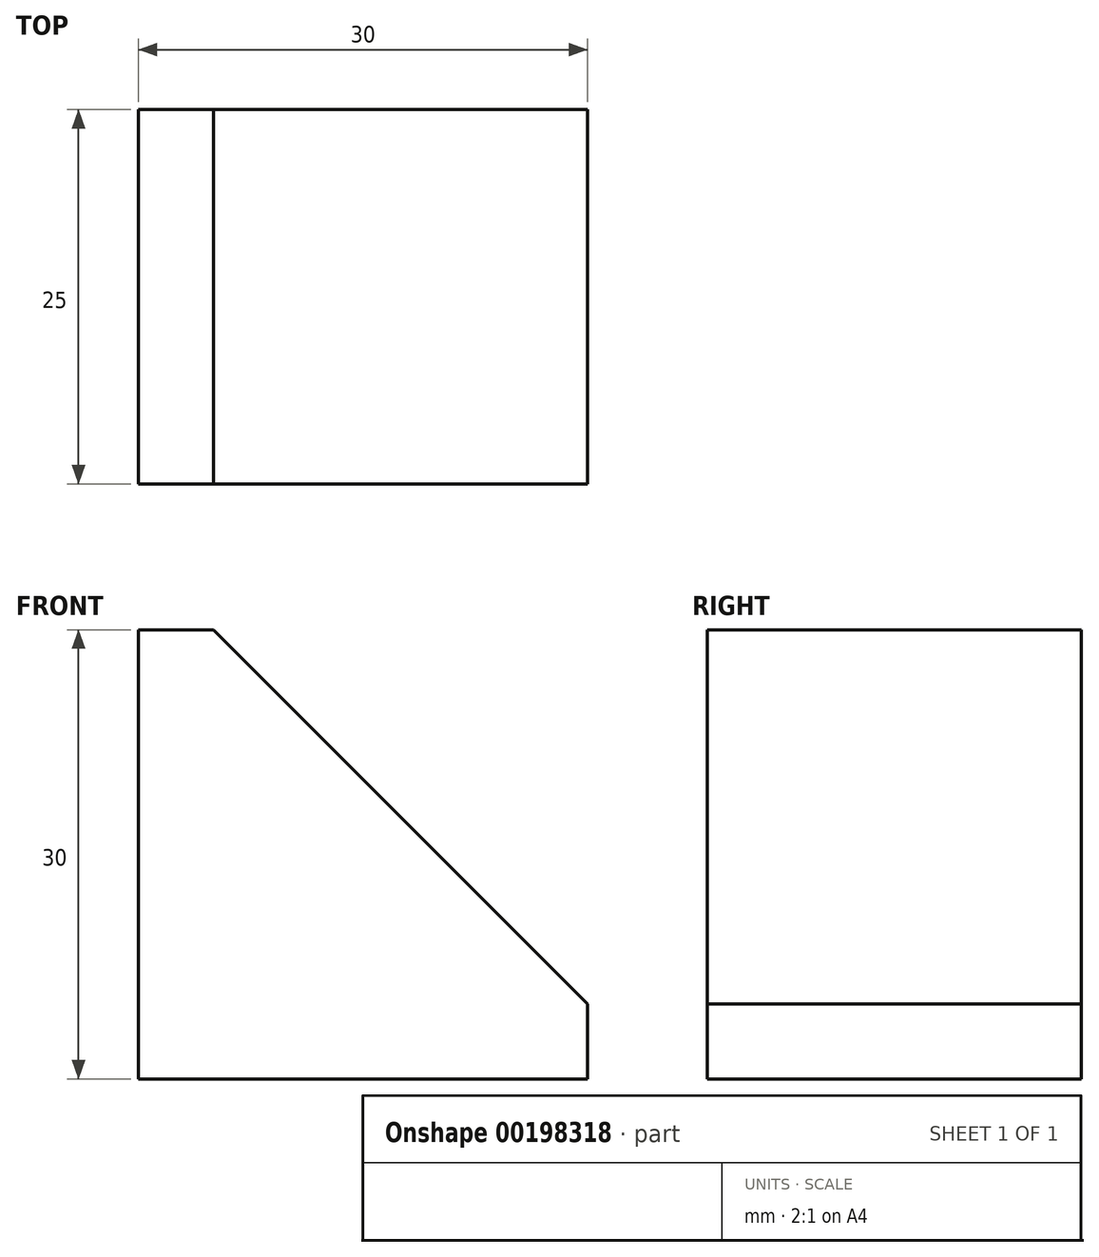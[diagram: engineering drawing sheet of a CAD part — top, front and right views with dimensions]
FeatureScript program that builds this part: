
annotation { "Feature Type Name" : "Feature", "Feature Type Description" : "" }
export const myFeature = defineFeature(function(context is Context, id is Id, definition is map)
    precondition{}
    {
        {
            var Q0;
            Q0=qCreatedBy(makeId("Front.planeOp"),FACE);
            var sketch = newSketch(context, id + "F0", { "sketchPlane" : qUnion([Q0])});
            skLineSegment(sketch, "E0", {"start": v(0, 0) * mm, "end": v(0, 30) * mm});
            skLineSegment(sketch, "E1", {"start": v(0, 30) * mm, "end": v(5, 30) * mm});
            skLineSegment(sketch, "E2", {"start": v(5, 30) * mm, "end": v(30, 5) * mm});
            skLineSegment(sketch, "E3", {"start": v(30, 5) * mm, "end": v(30, 0) * mm});
            skLineSegment(sketch, "E4", {"start": v(30, 0) * mm, "end": v(0, 0) * mm});
            skSolve(sketch);
        }
        {
            var Q0;
            Q0=qCreatedBy(makeId("Top.planeOp"),FACE);
            var sketch = newSketch(context, id + "F1", { "sketchPlane" : qUnion([Q0])});
            skLineSegment(sketch, "E5", {"start": v(0, 0) * mm, "end": v(30, 0) * mm});
            skLineSegment(sketch, "E6", {"start": v(30, 0) * mm, "end": v(30, 19) * mm});
            skLineSegment(sketch, "E7", {"start": v(30, 19) * mm, "end": v(0, 19) * mm});
            skLineSegment(sketch, "E8", {"start": v(0, 19) * mm, "end": v(0, 0) * mm});
            skCircle(sketch, "E9", {"center": v(20, 9.5) * mm, "radius": 3 * mm});
            skCircle(sketch, "E10", {"center": v(20, 9.5) * mm, "radius": 4.5 * mm});
            skLineSegment(sketch, "E11", {"start": v(15.5, 12) * mm, "end": v(0, 12) * mm});
            skLineSegment(sketch, "E12", {"start": v(0, 7) * mm, "end": v(15.5, 7) * mm});
            skLineSegment(sketch, "E13", {"start": v(15.5, 12) * mm, "end": v(15.5, 7) * mm});
            skLineSegment(sketch, "E14", {"start": v(0, 12) * mm, "end": v(0, 7) * mm});
            skSolve(sketch);
        }
        {
            var Q0;
            Q0=qCreatedBy(makeId("Top.planeOp"),FACE);
            cPlane(context, id + "F2", {"entities" : qUnion([Q0]), "cplaneType" : CPlaneType.OFFSET, "offset" : 30 * mm, "width" : 150 * mm, "height" : 150 * mm});
        }
        {
            var Q0;
            Q0=makeQuery(id+"F0.imprint","IMPRINT",FACE,{"disambiguationData":[TD([[makeQuery(id+"F0.imprint","IMPRINT",EDGE,{"derivedFrom":sQuery(id+"F0.wireOp",EDGE,"E0")}),-1.0]])]});
            extrude(context, id + "F3", {"entities" : qUnion([Q0]), "depth" : 25 * mm});
        }
    });
